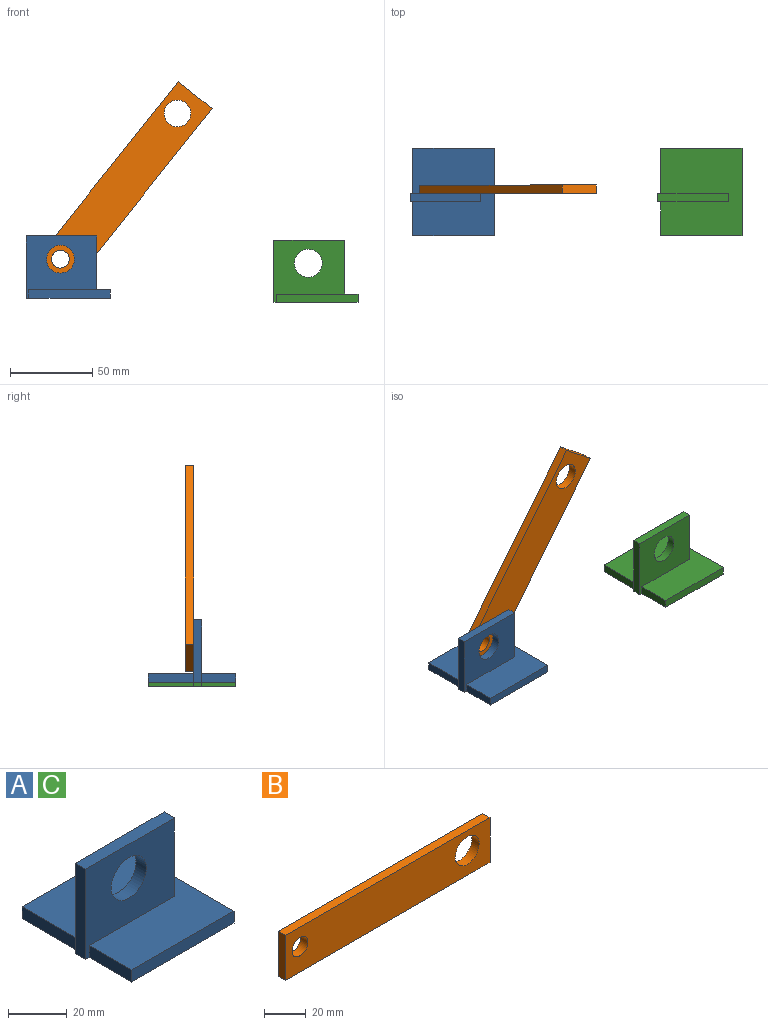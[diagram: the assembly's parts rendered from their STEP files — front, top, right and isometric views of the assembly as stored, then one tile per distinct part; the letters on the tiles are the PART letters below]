
ASSEMBLY  parts=3 mates=3
PART A: 13 faces, bbox 51.2x53.1x37.8 mm
  f0: plane 27.47x5mm, normal (-1,0,0), area 137.3mm2, adj f1,f5,f6,f8
  f1: plane 49.39x5mm, normal (0,1,0), area 246.9mm2, adj f0,f4,f5,f6
  f2: plane 20.61x5mm, normal (-1,0,0), area 103mm2, adj f3,f5,f6,f7
  f3: plane 49.39x5mm, normal (0,-1,0), area 246.9mm2, adj f2,f4,f5,f6
  f4: plane 53.08x5mm, normal (1,0,0), area 265.4mm2, adj f1,f3,f5,f6
  f5: plane 53.08x49.39mm, normal (0,0,1), area 2415.4mm2, adj f0,f1,f2,f3,f4,f7,f8,f10
  f6: plane 53.08x51.17mm, normal (0,0,-1), area 2630.4mm2, adj f0,f1,f2,f3,f4,f7,f8,f9
  f7: plane 43x37.76mm, normal (0,-1,0), area 1192mm2, adj f2,f5,f6,f9,f10,f11,f12
  f8: plane 43x37.76mm, normal (0,1,0), area 1192mm2, adj f0,f5,f6,f9,f10,f11,f12
  f9: plane 37.76x5mm, normal (-1,0,0), area 188.8mm2, adj f6,f7,f8,f11
  f10: plane 32.76x5mm, normal (1,0,0), area 163.8mm2, adj f5,f7,f8,f11
  f11: plane 43x5mm, normal (0,0,1), area 215mm2, adj f7,f8,f9,f10
  f12: cylinder r=8.48mm len=16.95mm, axis (0,1,0), area 266.3mm2, adj f7,f8
PART B: 8 faces, bbox 138.9x5x26.5 mm
  f0: plane 138.93x5mm, normal (0,0,1), area 694.6mm2, adj f1,f5,f6,f7
  f1: plane 26.46x5mm, normal (-1,0,0), area 132.3mm2, adj f0,f2,f6,f7
  f2: plane 138.93x5mm, normal (0,0,-1), area 694.6mm2, adj f1,f5,f6,f7
  f3: cylinder r=5.41mm len=10.83mm, axis (0,1,0), area 170mm2, adj f6,f7
  f4: cylinder r=8.12mm len=16.24mm, axis (0,1,0), area 255.1mm2, adj f6,f7
  f5: plane 26.24x5mm, normal (1,0,0), area 131.2mm2, adj f0,f2,f6,f7
  f6: plane 138.93x26.46mm, normal (0,-1,0), area 3361.7mm2, adj f0,f1,f2,f3,f4,f5
  f7: plane 138.93x26.46mm, normal (0,1,0), area 3361.7mm2, adj f0,f1,f2,f3,f4,f5
PART C: same geometry as A
PLACE A t=(-131.76,-61.03,-121.01)mm fixed
PLACE B rot(axis=(0,-1,0),51.4deg) t=(-53.25,-56.03,-34.05)mm
PLACE C t=(18.85,-61.03,-123.51)mm fixed
MATE planar C.f3 <-> A.f3  axis (0,-1,0) through (14.73,-86.64,-118.51)mm
MATE parallel C.f4 <-> A.f2  axis (1,0,0) through (39.42,-60.1,-121.01)mm
MATE revolute B.f3 <-> A.f12  axis (0,-1,0) through (-141.41,-61.03,-97.33)mm
